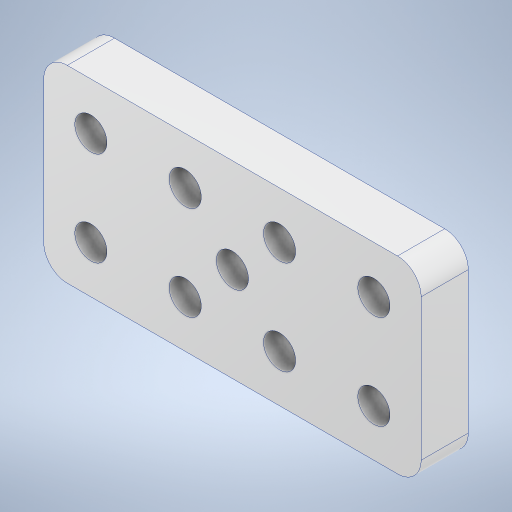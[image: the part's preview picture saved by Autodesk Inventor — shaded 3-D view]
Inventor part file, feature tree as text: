
AUTODESK INVENTOR PART (.ipt)
format: ipt  version: 2023 (Build 270158000, 158)  size: 264,192 bytes
history: native  units: in
note: dims shown in document units (in); Inventor stores cm internally (conversion verified against a paired STEP export)
features: extrude x1, fillet x1, sketch x1
ambient origin geometry x8: Origin, YZ Plane, XZ Plane, XY Plane, X Axis, Y Axis, Z Axis, Center Point
bodies: Solid1 (feature_tree)
feature tree (3):
  extrude  "Extrusion1"  Depth=1.5in
  fillet  "Fillet1"  Radius=0.5in
  sketch  "Sketch1"  dims[d0=0.17in d1=1.5in d9=0.5in d10=1.5748in d12=0.5in d13=0.7874in d15=0.5in d18=0.17in d19=1.0in d20=0.25in d21=0.0in d22=0.125in]
